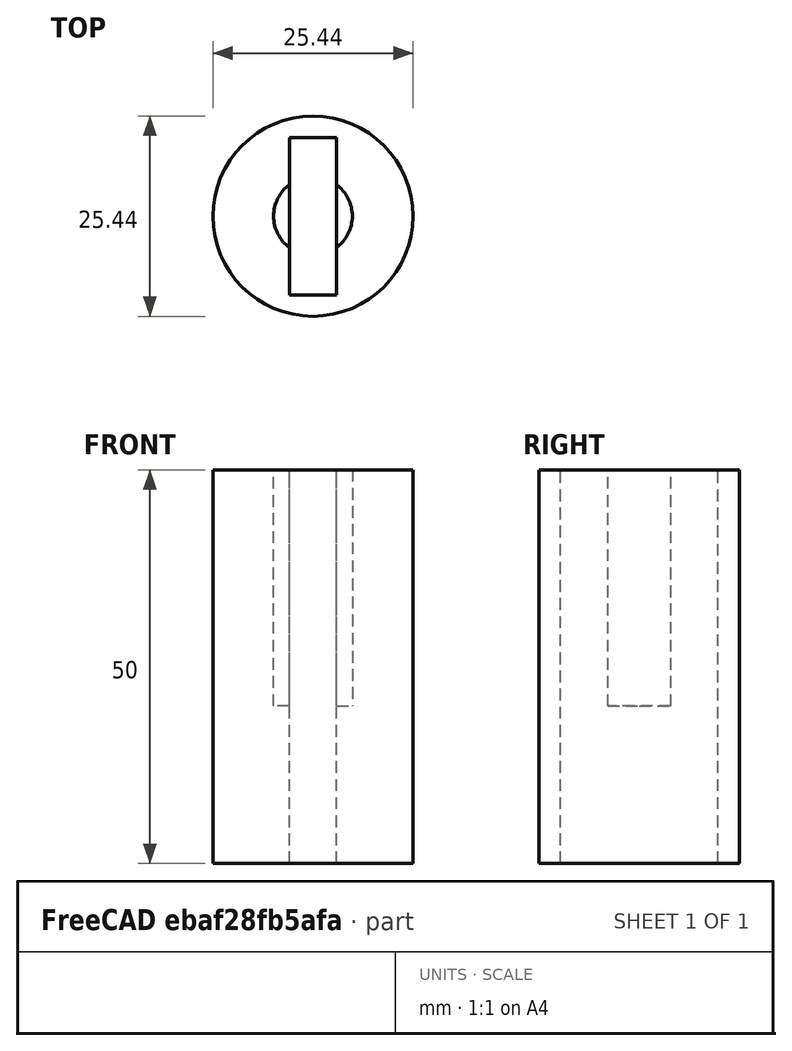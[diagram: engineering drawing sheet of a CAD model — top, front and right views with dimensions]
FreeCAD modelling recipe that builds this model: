
FCSTD DOCUMENT  (FreeCAD 0.20R29410 (Git))
Label: 1
License: All rights reserved
LicenseURL: http://en.wikipedia.org/wiki/All_rights_reserved
objects: Sketcher::SketchObject×2, PartDesign::Pad×1, PartDesign::Pocket×1, PartDesign::Body×1
note: 7 computed .brp shape members not serialized (recipe doc carries the construction recipe); baked Part::Feature solids carry a one-line shape summary decoded from their .brp

FEATURE [Sketcher::SketchObject] Sketch
  FullyConstrained = false
  MapMode = 5
  Support = -> [XY_Plane]
  sketch-geometry (5):
    g0: Circle CenterX=-51 CenterY=27 CenterZ=0 NormalX=0 NormalY=0 NormalZ=1 AngleXU=0 Radius=12.7152
    g1: LineSegment StartX=-54 StartY=37 StartZ=0 EndX=-48 EndY=37 EndZ=0
    g2: LineSegment StartX=-48 StartY=37 StartZ=0 EndX=-48 EndY=17 EndZ=0
    g3: LineSegment StartX=-48 StartY=17 StartZ=0 EndX=-54 EndY=17 EndZ=0
    g4: LineSegment StartX=-54 StartY=17 StartZ=0 EndX=-54 EndY=37 EndZ=0
  constraints (8):
    c: Coincident(g1,g2)
    c: Coincident(g2,g3)
    c: Coincident(g3,g4)
    c: Coincident(g4,g1)
    c: Horizontal(g1)
    c: Horizontal(g3)
    c: Vertical(g2)
    c: Vertical(g4)
FEATURE [PartDesign::Pad] Pad
  Direction = (0,0,1)
  Length = 50
  Length2 = 10
  Profile = -> Sketch
  ReferenceAxis = -> Sketch [N_Axis]
  Type = 0
FEATURE [Sketcher::SketchObject] Sketch001
  FullyConstrained = false
  MapMode = 5
  Placement = pos=(0,0,50) rot=(0,0,1;0rad)
  Support = -> [Pad]
  sketch-geometry (1):
    g0: Circle CenterX=-51 CenterY=27 CenterZ=0 NormalX=0 NormalY=0 NormalZ=1 AngleXU=0 Radius=5
FEATURE [PartDesign::Pocket] Pocket
  BaseFeature = -> Pad
  Direction = (0,0,-1)
  Length = 30
  Length2 = 5
  Profile = -> Sketch001
  ReferenceAxis = -> Sketch001 [N_Axis]
  Type = 0
FEATURE [PartDesign::Body] Body
  Group = -> [Sketch,Pad,Sketch001,Pocket]
  Origin = -> Origin
  Tip = -> Pocket
